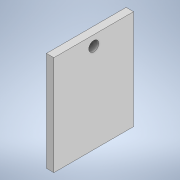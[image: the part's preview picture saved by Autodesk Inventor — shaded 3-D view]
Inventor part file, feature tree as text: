
AUTODESK INVENTOR PART (.ipt)
format: ipt  version: 2021 (Build 250183000, 183)  size: 110,592 bytes
history: native  units: in
note: dims shown in document units (in); Inventor stores cm internally (conversion verified against a paired STEP export)
features: reference x3, other x3, extrude x2, sketch x2, plane x1
ambient origin geometry x8: Origin, YZ Plane, XZ Plane, XY Plane, X Axis, Y Axis, Z Axis, Center Point
bodies: Solid1 (feature_tree)
feature tree (11):
  plane  "Work Plane1"
  extrude  "Extrusion1"  Depth=10.0in TaperAngle=0.0deg
  extrude  "Extrusion2"  Depth=1.0in
  sketch  "Sketch1"  dims[d0=0.75in d1=10.0in d2=0.0in]
  reference  "Reference1"
  reference  "Reference2"
  reference  "Reference3"
  sketch  "Sketch2"  dims[d3=1.0in d4=1.0in d5=0.0in d6=0.0in]
  parser-record x1  (decoder bookkeeping rows leaked as tree rows — omitted from the tree; the rows remain in map.json)
  other  "woodForkAssembly.iam"
  other  "woodForkSupportBase:1"
note: 1 file-system path scrubbed to <path> (originals preserved in map.json)
